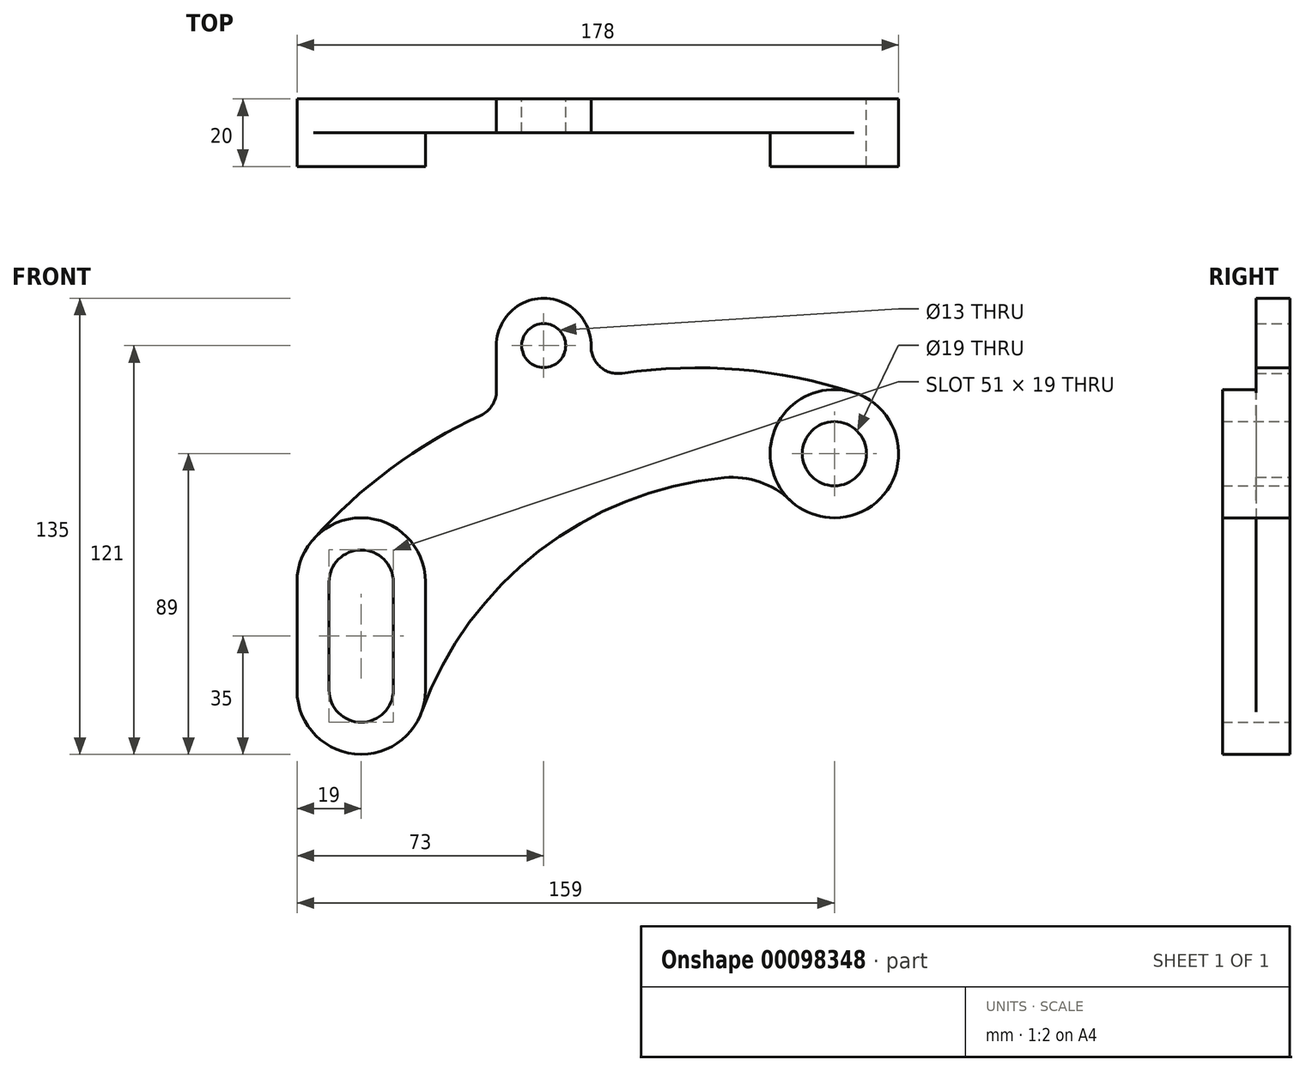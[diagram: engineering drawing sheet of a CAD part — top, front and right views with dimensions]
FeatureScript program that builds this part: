
annotation { "Feature Type Name" : "Feature", "Feature Type Description" : "" }
export const myFeature = defineFeature(function(context is Context, id is Id, definition is map)
    precondition{}
    {
        {
            var Q0;
            Q0=qCreatedBy(makeId("Front.planeOp"),FACE);
            var sketch = newSketch(context, id + "F0", { "sketchPlane" : qUnion([Q0])});
            skCircle(sketch, "E0", {"center": v(0, 0) * mm, "radius": 9.5 * mm});
            skCircle(sketch, "E1", {"center": v(0, 0) * mm, "radius": 19 * mm});
            skPoint(sketch, "E2", {"position": v(-86, 32) * mm});
            skCircle(sketch, "E3", {"center": v(-86, 32) * mm, "radius": 6.5 * mm});
            skArc(sketch, "E4", {"start": v(-72, 31.82) * mm, "mid": v(-85.91, 46) * mm, "end": v(-100, 32) * mm});
            skPoint(sketch, "E5", {"position": v(-140, -38) * mm});
            skPoint(sketch, "E6", {"position": v(-140, -70) * mm});
            skArc(sketch, "E7", {"start": v(-121, -38) * mm, "mid": v(-140, -19) * mm, "end": v(-159, -38) * mm});
            skArc(sketch, "E8", {"start": v(-130.5, -38) * mm, "mid": v(-140, -28.5) * mm, "end": v(-149.5, -38) * mm});
            skArc(sketch, "E9", {"start": v(-149.5, -70) * mm, "mid": v(-140, -79.5) * mm, "end": v(-130.5, -70) * mm});
            skLineSegment(sketch, "E10", {"start": v(-159, -38) * mm, "end": v(-159, -70) * mm});
            skLineSegment(sketch, "E11", {"start": v(-121, -38) * mm, "end": v(-121, -70) * mm});
            skLineSegment(sketch, "E12", {"start": v(-149.5, -38) * mm, "end": v(-149.5, -70) * mm});
            skLineSegment(sketch, "E13", {"start": v(-130.5, -38) * mm, "end": v(-130.5, -70) * mm});
            skArc(sketch, "E14.trimOffspring", {"start": v(-159, -70) * mm, "mid": v(-140, -89) * mm, "end": v(-121, -70) * mm});
            skArc(sketch, "E15", {"start": v(5.83, 18.08) * mm, "mid": v(-28.18, 24.89) * mm, "end": v(-62.84, 23.8) * mm});
            skArc(sketch, "E16", {"start": v(-104.64, 11.35) * mm, "mid": v(-101.26, 14.3) * mm, "end": v(-100, 18.61) * mm});
            skPoint(sketch, "E17", {"position": v(-154.17, -25.34) * mm});
            skLineSegment(sketch, "E18", {"start": v(-100, 32) * mm, "end": v(-100, 18.61) * mm});
            skArc(sketch, "E19", {"start": v(-62.84, 23.8) * mm, "mid": v(-69.27, 25.7) * mm, "end": v(-72, 31.82) * mm});
            skArc(sketch, "E20.trimOffspring", {"start": v(-104.64, 11.35) * mm, "mid": v(-131.29, -4.46) * mm, "end": v(-154.17, -25.34) * mm});
            skArc(sketch, "E21", {"start": v(-13.04, -13.82) * mm, "mid": v(-22.08, -8.35) * mm, "end": v(-32.58, -7.11) * mm});
            skArc(sketch, "E22", {"start": v(-32.58, -7.11) * mm, "mid": v(-87.4, -28.83) * mm, "end": v(-122.14, -76.48) * mm});
            skSolve(sketch);
        }
        {
            var Q0;
            Q0=makeQuery(id+"F0.imprint","IMPRINT",FACE,{"disambiguationData":[TD([[makeQuery(id+"F0.imprint","IMPRINT",EDGE,{"derivedFrom":sQuery(id+"F0.wireOp",EDGE,"E3")}),-1.0]])]});
            extrude(context, id + "F1", {"entities" : qUnion([Q0]), "depth" : 10 * mm});
        }
        {
            var Q0;
            Q0=makeQuery(id+"F0.imprint","IMPRINT",FACE,{"disambiguationData":[TD([[makeQuery(id+"F0.imprint","IMPRINT",EDGE,{"derivedFrom":sQuery(id+"F0.wireOp",EDGE,"E8")}),-1.0]])]});
            var Q1;
            Q1=makeQuery(id+"F0.imprint","IMPRINT",FACE,{"disambiguationData":[TD([[makeQuery(id+"F0.imprint","IMPRINT",EDGE,{"derivedFrom":sQuery(id+"F0.wireOp",EDGE,"E0")}),-1.0]])]});
            extrude(context, id + "F2", {"entities" : qUnion([Q0, Q1]), "operationType" : NewBodyOperationType.ADD, "depth" : 20 * mm});
        }
    });
